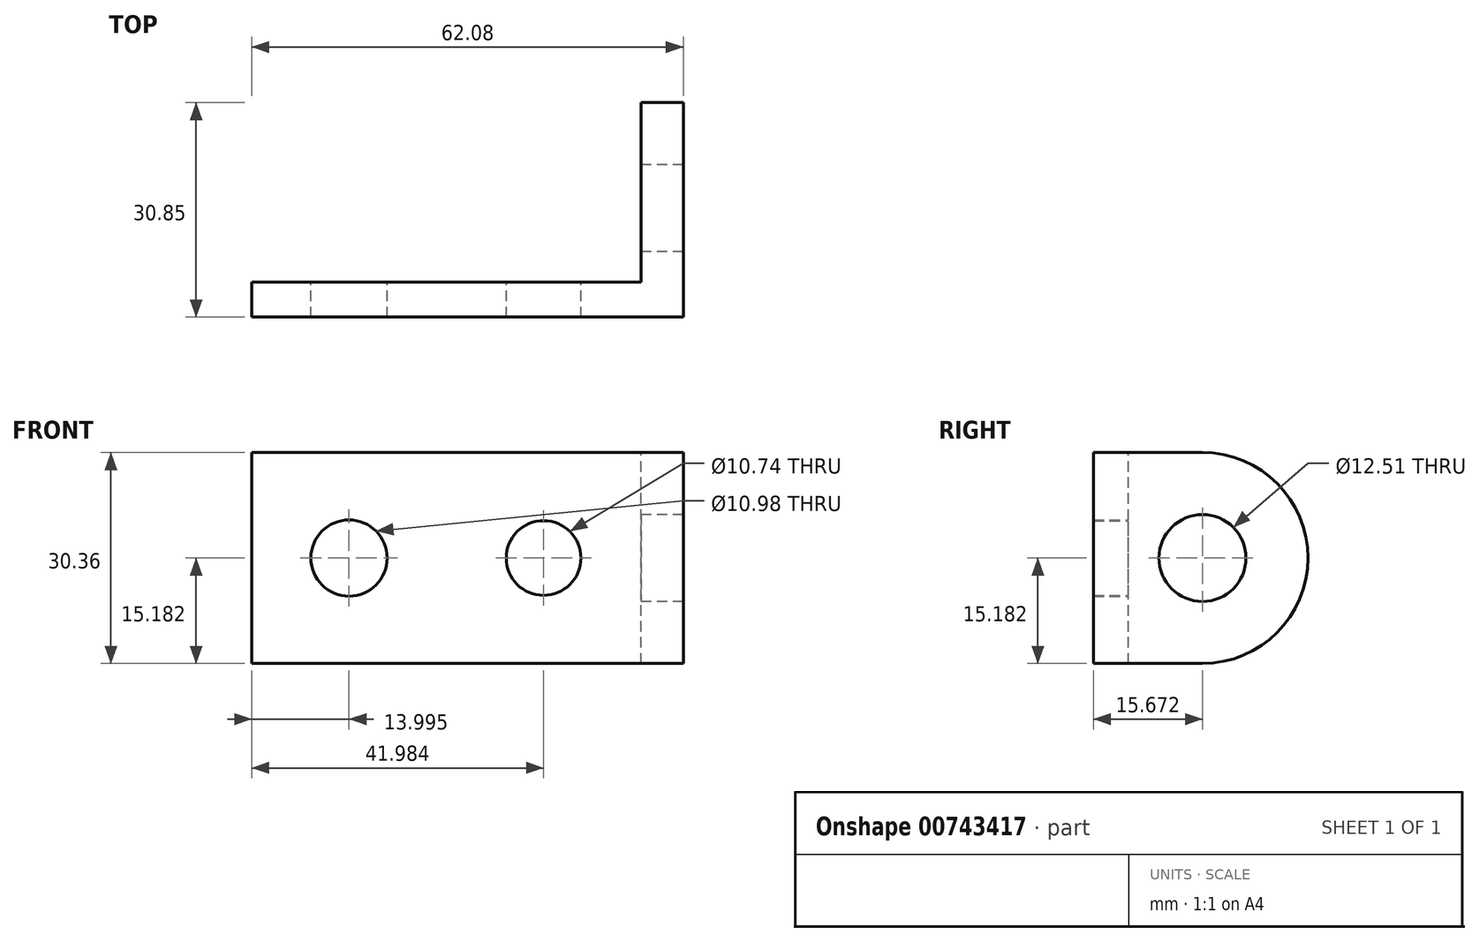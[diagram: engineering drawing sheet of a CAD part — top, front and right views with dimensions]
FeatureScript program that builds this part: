
annotation { "Feature Type Name" : "Feature", "Feature Type Description" : "" }
export const myFeature = defineFeature(function(context is Context, id is Id, definition is map)
    precondition{}
    {
        {
            var Q0;
            Q0=qCreatedBy(makeId("Front.planeOp"),FACE);
            var sketch = newSketch(context, id + "F0", { "sketchPlane" : qUnion([Q0])});
            skLineSegment(sketch, "E0.bottom", {"start": v(0, 0) * mm, "end": v(55.98, 0) * mm});
            skLineSegment(sketch, "E0.top", {"start": v(0, 30.36) * mm, "end": v(55.98, 30.36) * mm});
            skLineSegment(sketch, "E0.left", {"start": v(0, 0) * mm, "end": v(0, 30.36) * mm});
            skLineSegment(sketch, "E0.right", {"start": v(55.98, 0) * mm, "end": v(55.98, 30.36) * mm});
            skCircle(sketch, "E1", {"center": v(41.98, 15.18) * mm, "radius": 5.37 * mm});
            skCircle(sketch, "E2", {"center": v(14, 15.18) * mm, "radius": 5.49 * mm});
            skSolve(sketch);
        }
        {
            var Q0;
            Q0 = qSketchRegion(id + "F0", true);
            extrude(context, id + "F1", {"entities" : qUnion([Q0]), "depth" : 5 * mm, "offsetDistance" : 25 * mm});
        }
        {
            var Q0;
            Q0=makeQuery(id+"F1.opExtrude","SWEPT_FACE",FACE,{"disambiguationData":[OSD([sQuery(id+"F0.wireOp",EDGE,"E0.right")])]});
            var sketch = newSketch(context, id + "F2", { "sketchPlane" : qUnion([Q0])});
            skLineSegment(sketch, "E3", {"start": v(0, 30.36) * mm, "end": v(10.67, 30.36) * mm});
            skLineSegment(sketch, "E4", {"start": v(0, 0) * mm, "end": v(10.67, 0) * mm});
            skLineSegment(sketch, "E5", {"start": v(0, 0) * mm, "end": v(-5, 0) * mm});
            skLineSegment(sketch, "E6", {"start": v(-5, 0) * mm, "end": v(-5, 30.36) * mm});
            skLineSegment(sketch, "E7", {"start": v(-5, 30.36) * mm, "end": v(0, 30.36) * mm});
            skArc(sketch, "E8", {"start": v(10.67, 0) * mm, "mid": v(25.85, 15.18) * mm, "end": v(10.67, 30.36) * mm});
            skSolve(sketch);
        }
        {
            var Q0;
            Q0 = qSketchRegion(id + "F2", true);
            extrude(context, id + "F3", {"entities" : qUnion([Q0]), "operationType" : NewBodyOperationType.ADD, "depth" : 6.1 * mm, "offsetDistance" : 25 * mm});
        }
        {
            var Q0;
            Q0=makeQuery(id+"F3.opExtrude","CAP_FACE",FACE,{"disambiguationData":[OSD([sQuery(id+"F2.wireOp",EDGE,"E3"),sQuery(id+"F2.wireOp",EDGE,"E4"),sQuery(id+"F2.wireOp",EDGE,"E5"),sQuery(id+"F2.wireOp",EDGE,"E6"),sQuery(id+"F2.wireOp",EDGE,"E7"),sQuery(id+"F2.wireOp",EDGE,"E8")])],"isStart":true});
            var sketch = newSketch(context, id + "F4", { "sketchPlane" : qUnion([Q0])});
            skCircle(sketch, "E9", {"center": v(-10.67, 15.18) * mm, "radius": 6.25 * mm});
            skSolve(sketch);
        }
        {
            var Q0;
            Q0 = qSketchRegion(id + "F4", true);
            extrude(context, id + "F5", {"entities" : qUnion([Q0]), "operationType" : NewBodyOperationType.REMOVE, "oppositeDirection" : true, "depth" : 25 * mm, "offsetDistance" : 25 * mm});
        }
    });
